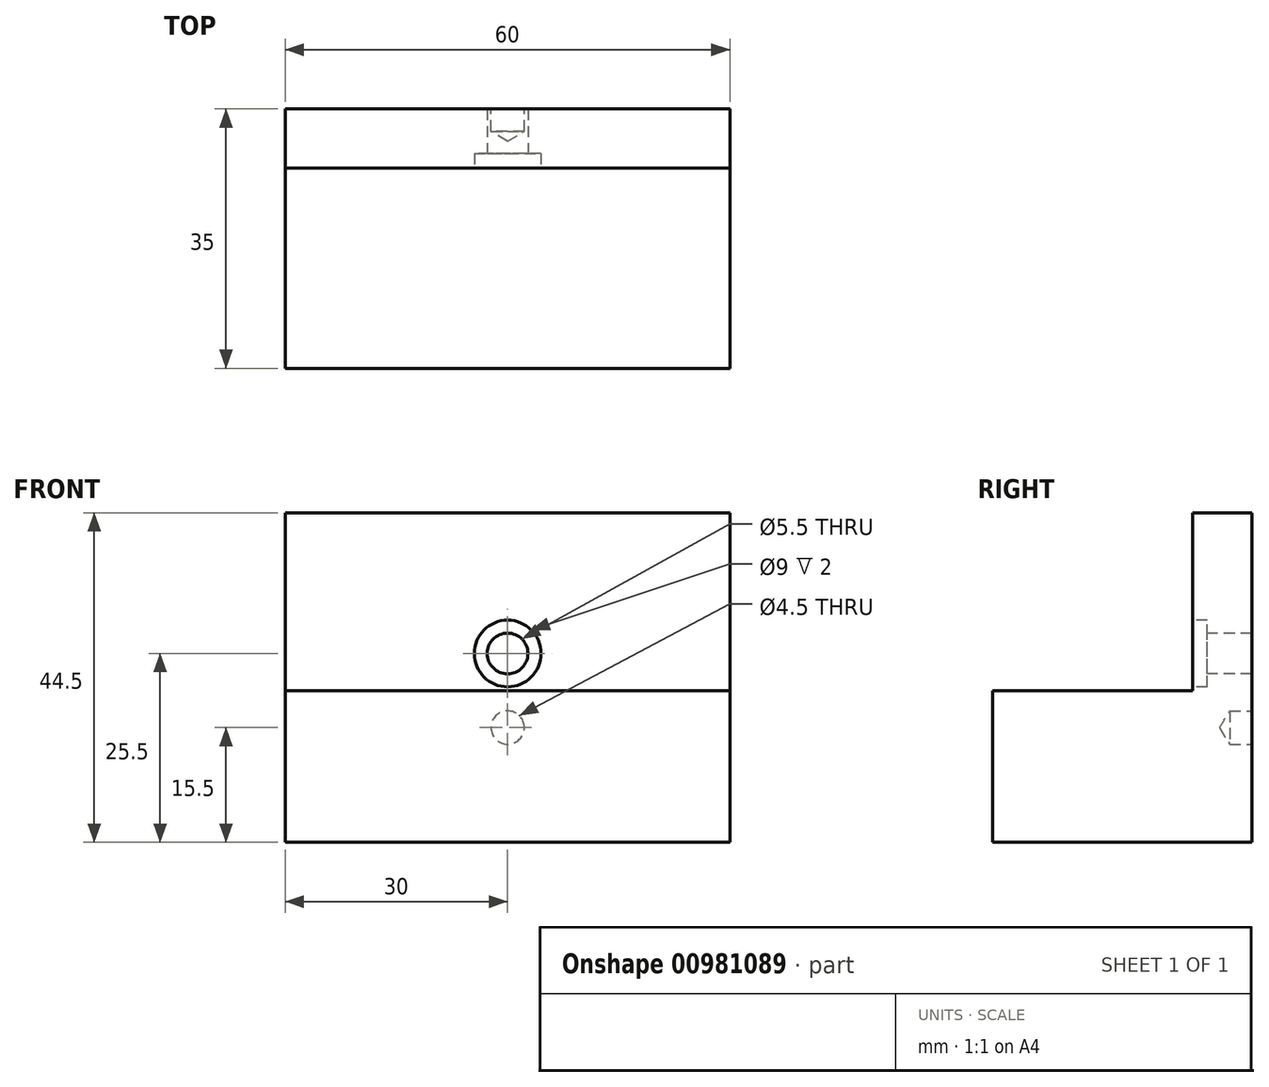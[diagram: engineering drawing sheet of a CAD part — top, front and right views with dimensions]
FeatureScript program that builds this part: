
annotation { "Feature Type Name" : "Feature", "Feature Type Description" : "" }
export const myFeature = defineFeature(function(context is Context, id is Id, definition is map)
    precondition{}
    {
        {
            var Q0;
            Q0=qCreatedBy(makeId("Top.planeOp"),FACE);
            var sketch = newSketch(context, id + "F0", { "sketchPlane" : qUnion([Q0])});
            skLineSegment(sketch, "E0.bottom", {"start": v(30, -17.5) * mm, "end": v(-30, -17.5) * mm});
            skLineSegment(sketch, "E0.top", {"start": v(30, 17.5) * mm, "end": v(-30, 17.5) * mm});
            skLineSegment(sketch, "E0.left", {"start": v(30, -17.5) * mm, "end": v(30, 17.5) * mm});
            skLineSegment(sketch, "E0.right", {"start": v(-30, -17.5) * mm, "end": v(-30, 17.5) * mm});
            skPoint(sketch, "E0.middle", {"position": v(0, 0) * mm});
            skSolve(sketch);
        }
        {
            var Q0;
            Q0 = qSketchRegion(id + "F0", true);
            extrude(context, id + "F1", {"entities" : qUnion([Q0]), "depth" : 20.5 * mm, "offsetDistance" : 25 * mm});
        }
        {
            var Q0;
            Q0=makeQuery(id+"F1.opExtrude","CAP_FACE",FACE,{"disambiguationData":[OSD([sQuery(id+"F0.wireOp",EDGE,"E0.bottom"),sQuery(id+"F0.wireOp",EDGE,"E0.top"),sQuery(id+"F0.wireOp",EDGE,"E0.left"),sQuery(id+"F0.wireOp",EDGE,"E0.right")])],"isStart":false});
            var sketch = newSketch(context, id + "F2", { "sketchPlane" : qUnion([Q0])});
            skLineSegment(sketch, "E1.bottom", {"start": v(-30, 17.5) * mm, "end": v(30, 17.5) * mm});
            skLineSegment(sketch, "E1.top", {"start": v(-30, 9.5) * mm, "end": v(30, 9.5) * mm});
            skLineSegment(sketch, "E1.left", {"start": v(-30, 17.5) * mm, "end": v(-30, 9.5) * mm});
            skLineSegment(sketch, "E1.right", {"start": v(30, 17.5) * mm, "end": v(30, 9.5) * mm});
            skSolve(sketch);
        }
        {
            var Q0;
            Q0 = qSketchRegion(id + "F2", true);
            extrude(context, id + "F3", {"entities" : qUnion([Q0]), "operationType" : NewBodyOperationType.ADD, "depth" : 24 * mm, "offsetDistance" : 25 * mm});
        }
        {
            var Q0;
            Q0=makeQuery(id+"F3.opExtrude","SWEPT_FACE",FACE,{"disambiguationData":[OSD([sQuery(id+"F2.wireOp",EDGE,"E1.top")])]});
            var sketch = newSketch(context, id + "F4", { "sketchPlane" : qUnion([Q0])});
            skPoint(sketch, "E2", {"position": v(0, 25.5) * mm});
            skLineSegment(sketch, "E3", {"start": v(0, 25.5) * mm, "end": v(30, 25.5) * mm, "construction": true});
            skLineSegment(sketch, "E4", {"start": v(0, 25.5) * mm, "end": v(-30, 25.5) * mm, "construction": true});
            skSolve(sketch);
        }
        {
            var Q0;
            Q0=sQuery(id+"F4.wireOp",VERTEX,"E2");
            var Q1;
            Q1=makeQuery(id+"F1.opExtrude","SWEPT_BODY",BODY,{"disambiguationData":[OSD([sQuery(id+"F0.wireOp",EDGE,"E0.bottom"),sQuery(id+"F0.wireOp",EDGE,"E0.top"),sQuery(id+"F0.wireOp",EDGE,"E0.left"),sQuery(id+"F0.wireOp",EDGE,"E0.right")])]});
            hole(context, id + "F5", {"style" : HoleStyle.C_BORE, "endStyle" : HoleEndStyle.THROUGH, "holeDiameter" : 5.5 * mm, "cBoreDiameter" : 9 * mm, "cBoreDepth" : 2 * mm, "majorDiameter" : 5 * mm, "isTappedThrough" : true, "tappedDepth" : 12 * mm, "tapClearance" : 3, "locations" : qUnion([Q0]), "scope" : qUnion([Q1])});
        }
        {
            var Q0;
            Q0=makeQuery(id+"F3.boolean.opBoolean","MERGE",FACE,{"derivedFrom":[makeQuery(id+"F1.opExtrude","SWEPT_FACE",FACE,{"disambiguationData":[OSD([sQuery(id+"F0.wireOp",EDGE,"E0.top")])]}),makeQuery(id+"F3.opExtrude","SWEPT_FACE",FACE,{"disambiguationData":[OSD([sQuery(id+"F2.wireOp",EDGE,"E1.bottom")])]})]});
            var sketch = newSketch(context, id + "F6", { "sketchPlane" : qUnion([Q0])});
            skPoint(sketch, "E5", {"position": v(0, 15.5) * mm});
            skPoint(sketch, "E6", {"position": v(9.58, 44.5) * mm});
            skSolve(sketch);
        }
        {
            var Q0;
            Q0=sQuery(id+"F6.wireOp",VERTEX,"E5");
            var Q1;
            Q1=makeQuery(id+"F1.opExtrude","SWEPT_BODY",BODY,{"disambiguationData":[OSD([sQuery(id+"F0.wireOp",EDGE,"E0.bottom"),sQuery(id+"F0.wireOp",EDGE,"E0.top"),sQuery(id+"F0.wireOp",EDGE,"E0.left"),sQuery(id+"F0.wireOp",EDGE,"E0.right")])]});
            hole(context, id + "F7", {"style" : HoleStyle.SIMPLE, "endStyle" : HoleEndStyle.BLIND, "standardTappedOrClearance" : lookupTablePath({ "fit" : "Normal", "standard" : "ISO", "size" : "M4", "type" : "Clearance" }), "standardBlindInLast" : lookupTablePath({ "fit" : "Normal", "standard" : "ISO", "engagement" : "75%", "pitch" : "0.7 mm", "size" : "M4", "type" : "Clearance & tapped" }), "holeDiameter" : 4.5 * mm, "majorDiameter" : 5 * mm, "holeDepth" : 3 * mm, "isTappedThrough" : true, "tappedDepth" : 12 * mm, "tapClearance" : 3, "locations" : qUnion([Q0]), "scope" : qUnion([Q1])});
        }
    });
